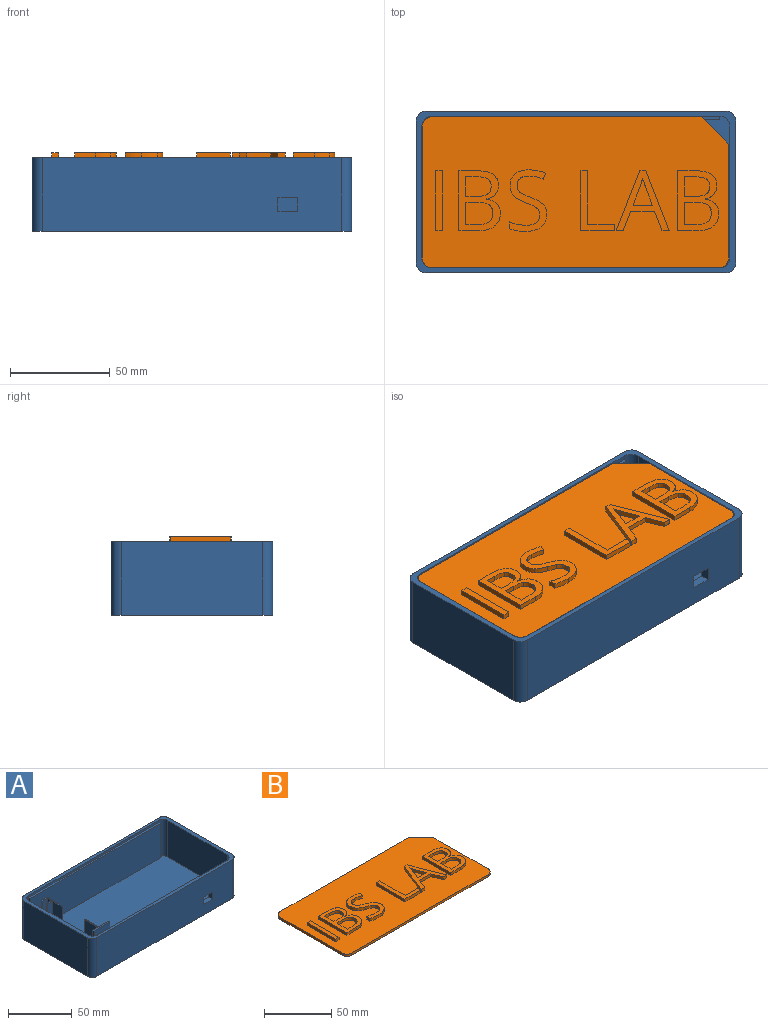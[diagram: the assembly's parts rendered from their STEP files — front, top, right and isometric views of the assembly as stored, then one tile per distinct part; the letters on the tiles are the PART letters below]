
ASSEMBLY  parts=2 mates=1
PART A: 56 faces, bbox 160x81x37 mm
  f0: plane 144x2mm, normal (0,-1,0), area 288mm2, adj f17,f23,f24,f44
  f1: plane 16.12x5.6mm, normal (0,-1,0), area 90.3mm2, adj f2,f7,f8,f42
  f2: plane 16.12x1.15mm, normal (-1,0,0), area 18.5mm2, adj f1,f8,f37,f42
  f3: plane 5.6x4.3mm, normal (0,1,0), area 24.1mm2, adj f5,f7,f39,f43
  f4: plane 154x76mm, normal (0,0,1), area 10793mm2, adj f5,f6,f19,f21,f22,f23,f24,f25
  f5: plane 58.35x30mm, normal (-1,0,0), area 231.4mm2, adj f3,f4,f8,f28,f29,f31,f32,f34
  f6: plane 30x17.4mm, normal (1,0,0), area 522mm2, adj f4,f8,f28,f35
  f7: plane 29x16.6mm, normal (-1,0,0), area 436.7mm2, adj f1,f3,f8,f29,f35,f37,f38,f39
  f8: plane 17.4x6.4mm, normal (0,0,1), area 24.8mm2, adj f1,f2,f5,f6,f7,f28,f35,f37
  f9: plane 71x37mm, normal (-1,0,0), area 2627mm2, adj f10,f16,f17,f18
  f10: cylinder r=5mm len=37mm, axis (0,0,-1), area 290.6mm2, adj f9,f11,f17,f18
  f11: plane 150x37mm, normal (0,-1,0), area 5480mm2, adj f10,f12,f17,f18,f52,f53,f54,f55
  f12: cylinder r=5mm len=37mm, axis (0,0,-1), area 290.6mm2, adj f11,f13,f17,f18
  f13: plane 71x37mm, normal (1,0,0), area 2627mm2, adj f12,f14,f17,f18
  f14: cylinder r=5mm len=37mm, axis (0,0,-1), area 290.6mm2, adj f13,f15,f17,f18
  f15: plane 150x37mm, normal (0,1,0), area 5550mm2, adj f14,f16,f17,f18
  f16: cylinder r=5mm len=37mm, axis (0,0,-1), area 290.6mm2, adj f9,f15,f17,f18
  f17: plane 160x81mm, normal (0,0,1), area 1256mm2, adj f0,f9,f10,f11,f12,f13,f14,f15
  f18: plane 160x81mm, normal (0,0,-1), area 12938.5mm2, adj f9,f10,f11,f12,f13,f14,f15,f16
  f19: cylinder r=5mm len=35mm, axis (0,0,1), area 274.9mm2, adj f4,f17,f20,f25,f50
  f20: plane 144x2mm, normal (0,1,0), area 288mm2, adj f17,f19,f21,f48
  f21: cylinder r=5mm len=35mm, axis (0,0,1), area 274.9mm2, adj f4,f17,f20,f22,f49
  f22: plane 66x35mm, normal (-1,0,0), area 2310mm2, adj f4,f17,f21,f23
  f23: cylinder r=5mm len=35mm, axis (0,0,1), area 274.9mm2, adj f0,f4,f17,f22,f46
  f24: cylinder r=5mm len=35mm, axis (0,0,1), area 274.9mm2, adj f0,f4,f17,f25,f45
  f25: plane 66x35mm, normal (1,0,0), area 2310mm2, adj f4,f17,f19,f24
  f26: plane 30x11.2mm, normal (0,1,0), area 336mm2, adj f4,f27,f33,f34
  f27: plane 30x14.9mm, normal (1,0,0), area 446.8mm2, adj f4,f26,f34,f36
  f28: plane 30x6.4mm, normal (0,1,0), area 192mm2, adj f4,f5,f6,f8
  f29: plane 5.6x2.3mm, normal (0,-1,0), area 12.9mm2, adj f5,f7,f41,f43
  f30: plane 27x14.9mm, normal (-1,0,0), area 402.2mm2, adj f31,f34,f36,f41
  f31: plane 27x5.6mm, normal (0,1,0), area 151.2mm2, adj f5,f30,f34,f41
  f32: plane 30x17.6mm, normal (0,-1,0), area 528mm2, adj f4,f5,f33,f34
  f33: plane 30x1.55mm, normal (1,0,0), area 46.5mm2, adj f4,f26,f32,f34
  f34: plane 17.6x16.44mm, normal (0,0,1), area 39.2mm2, adj f5,f26,f27,f30,f31,f32,f33,f36
  f35: plane 30x0.8mm, normal (0,-1,0), area 24mm2, adj f4,f6,f7,f8,f40
  f36: plane 30x0.8mm, normal (0,1,0), area 24mm2, adj f4,f27,f30,f34,f40
  f37: plane 16.12x5.6mm, normal (0,1,0), area 90.3mm2, adj f2,f7,f8,f42
  f38: plane 29x5.6mm, normal (0,-1,0), area 162.4mm2, adj f5,f7,f8,f39
  f39: plane 5.6x4.85mm, normal (0,0,1), area 27.2mm2, adj f3,f5,f7,f38
  f40: plane 24.51x3mm, normal (1,0,0), area 73.5mm2, adj f4,f35,f36,f41
  f41: plane 50x5.6mm, normal (0,0,1), area 280mm2, adj f5,f7,f29,f30,f31,f40
  f42: plane 5.6x1.15mm, normal (0,0,-1), area 6.4mm2, adj f1,f2,f7,f37
  f43: plane 5.6x1.15mm, normal (0,0,1), area 6.4mm2, adj f3,f5,f7,f29
  f44: plane 144x1.8mm, normal (0,0,1), area 259.2mm2, adj f0,f45,f46,f47
  f45: plane 33x1.8mm, normal (-1,0,0), area 59.4mm2, adj f4,f24,f44,f47
  f46: plane 33x1.8mm, normal (1,0,0), area 59.4mm2, adj f4,f23,f44,f47
  f47: plane 144x33mm, normal (0,-1,0), area 4752mm2, adj f4,f44,f45,f46
  f48: plane 144x1.8mm, normal (0,0,1), area 259.2mm2, adj f20,f49,f50,f51
  f49: plane 33x1.8mm, normal (1,0,0), area 59.4mm2, adj f4,f21,f48,f51
  f50: plane 33x1.8mm, normal (-1,0,0), area 59.4mm2, adj f4,f19,f48,f51
  f51: plane 144x33mm, normal (0,1,0), area 4682mm2, adj f4,f48,f49,f50,f52,f53,f54,f55
  f52: plane 7x4.3mm, normal (-1,0,0), area 30.1mm2, adj f11,f51,f53,f55
  f53: plane 10x4.3mm, normal (0,0,-1), area 43mm2, adj f11,f51,f52,f54
  f54: plane 7x4.3mm, normal (1,0,0), area 30.1mm2, adj f11,f51,f53,f55
  f55: plane 10x4.3mm, normal (0,0,1), area 43mm2, adj f11,f51,f52,f54
PART B: 119 faces, bbox 153.6x75.6x4.5 mm
  f0: plane 153.6x75.6mm, normal (0,0,1), area 9639.9mm2, adj f1,f2,f3,f4,f5,f6,f7,f8
  f1: plane 65.6x2mm, normal (-1,0,0), area 131.2mm2, adj f0,f2,f8,f9
  f2: cylinder r=5mm len=5mm, axis (0,0,-1), area 15.7mm2, adj f0,f1,f3,f9
  f3: plane 143.6x2mm, normal (0,-1,0), area 287.2mm2, adj f0,f2,f4,f9
  f4: cylinder r=5mm len=5mm, axis (0,0,-1), area 15.7mm2, adj f0,f3,f5,f9
  f5: plane 57.03x2mm, normal (1,0,0), area 114.1mm2, adj f0,f4,f6,f9
  f6: plane 13.57x13.32mm, normal (0.71,0.7,0), area 38mm2, adj f0,f5,f7,f9
  f7: plane 135.28x2mm, normal (0,1,0), area 270.6mm2, adj f0,f6,f8,f9
  f8: cylinder r=5mm len=5mm, axis (0,0,-1), area 15.7mm2, adj f0,f1,f7,f9
  f9: plane 153.6x75.6mm, normal (0,0,-1), area 11505.7mm2, adj f1,f2,f3,f4,f5,f6,f7,f8
  f10: plane 3.48x2.5mm, normal (0,-1,0), area 8.7mm2, adj f0,f11,f13,f14
  f11: plane 29.94x2.5mm, normal (1,0,0), area 74.9mm2, adj f0,f10,f12,f14
  f12: plane 3.48x2.5mm, normal (0,1,0), area 8.7mm2, adj f0,f11,f13,f14
  f13: plane 29.94x2.5mm, normal (-1,0,0), area 74.9mm2, adj f0,f10,f12,f14
  f14: plane 29.94x3.48mm, normal (0,0,1), area 104.2mm2, adj f10,f11,f12,f13
  f15: plane 29.94x2.5mm, normal (-1,0,0), area 74.9mm2, adj f0,f16,f39,f40
  f16: plane 10.45x2.5mm, normal (0,-1,0), area 26.1mm2, adj f0,f15,f17,f40
  f17: extruded ~7.59x2.5mm, area 20.2mm2, adj f0,f16,f18,f40
  f18: extruded ~6.27x2.71mm, area 17.7mm2, adj f0,f17,f19,f40
  f19: extruded ~7.17x6.82mm, area 27.4mm2, adj f0,f18,f20,f40
  f20: plane 2.5x0.2mm, normal (1,0,0), area 0.5mm2, adj f0,f19,f21,f40
  f21: extruded ~4.34x2.5mm, area 12.4mm2, adj f0,f20,f22,f40
  f22: extruded ~4.4x2.5mm, area 11.9mm2, adj f0,f21,f23,f40
  f23: extruded ~5.63x2.66mm, area 16.3mm2, adj f0,f22,f24,f40
  f24: extruded ~8.62x2.5mm, area 22.3mm2, adj f0,f23,f39,f40
  f25: plane 9.8x2.5mm, normal (1,0,0), area 24.5mm2, adj f26,f37,f40,f42
  f26: plane 5.12x2.5mm, normal (0,-1,0), area 12.8mm2, adj f25,f27,f40,f42
  f27: extruded ~5.73x2.5mm, area 14.8mm2, adj f26,f28,f40,f42
  f28: extruded ~3.64x2.5mm, area 10.6mm2, adj f27,f29,f40,f42
  f29: extruded ~3.9x2.5mm, area 11mm2, adj f28,f30,f40,f42
  f30: extruded ~5.31x2.5mm, area 13.8mm2, adj f29,f37,f40,f42
  f31: plane 5.96x2.5mm, normal (0,-1,0), area 14.9mm2, adj f32,f38,f40,f41
  f32: extruded ~5.7x2.5mm, area 14.8mm2, adj f31,f33,f40,f41
  f33: extruded ~4.1x2.5mm, area 11.7mm2, adj f32,f34,f40,f41
  f34: extruded ~4.4x2.5mm, area 12.4mm2, adj f33,f35,f40,f41
  f35: extruded ~5.46x2.5mm, area 14.3mm2, adj f34,f36,f40,f41
  f36: plane 6.25x2.5mm, normal (0,1,0), area 15.6mm2, adj f35,f38,f40,f41
  f37: plane 5.73x2.5mm, normal (0,1,0), area 14.3mm2, adj f25,f30,f40,f42
  f38: plane 11.21x2.5mm, normal (1,0,0), area 28mm2, adj f31,f36,f40,f41
  f39: plane 8.46x2.5mm, normal (0,1,0), area 21.2mm2, adj f0,f15,f24,f40
  f40: plane 29.94x20.75mm, normal (0,0,1), area 305.7mm2, adj f15,f16,f17,f18,f19,f20,f21,f22
  f41: plane 13.54x11.21mm, normal (0,0,1), area 138.2mm2, adj f31,f32,f33,f34,f35,f36,f38
  f42: plane 12.66x9.8mm, normal (0,0,1), area 113.4mm2, adj f25,f26,f27,f28,f29,f30,f37
  f43: extruded ~4.99x2.5mm, area 13.6mm2, adj f0,f44,f67,f68
  f44: extruded ~6.48x3.6mm, area 18.7mm2, adj f0,f43,f45,f68
  f45: extruded ~4.17x2.5mm, area 11.4mm2, adj f0,f44,f46,f68
  f46: extruded ~2.5x1.94mm, area 6.7mm2, adj f0,f45,f47,f68
  f47: extruded ~2.55x2.5mm, area 6.6mm2, adj f0,f46,f48,f68
  f48: extruded ~3.3x2.5mm, area 9.5mm2, adj f0,f47,f49,f68
  f49: extruded ~4.32x2.5mm, area 11.4mm2, adj f0,f48,f50,f68
  f50: extruded ~7.21x2.5mm, area 18.6mm2, adj f0,f49,f51,f68
  f51: plane 3.03x2.5mm, normal (0.94,-0.34,0), area 8mm2, adj f0,f50,f52,f68
  f52: extruded ~8.21x2.5mm, area 21.1mm2, adj f0,f51,f53,f68
  f53: extruded ~6.88x2.5mm, area 18.3mm2, adj f0,f52,f54,f68
  f54: extruded ~5.51x2.6mm, area 15.8mm2, adj f0,f53,f55,f68
  f55: extruded ~5.34x2.5mm, area 14.4mm2, adj f0,f54,f56,f68
  f56: extruded ~5.97x3.54mm, area 17.5mm2, adj f0,f55,f57,f68
  f57: extruded ~4.45x2.5mm, area 12.1mm2, adj f0,f56,f58,f68
  f58: extruded ~2.5x2.09mm, area 7mm2, adj f0,f57,f59,f68
  f59: extruded ~2.55x2.5mm, area 6.6mm2, adj f0,f58,f60,f68
  f60: extruded ~3.68x2.5mm, area 10.6mm2, adj f0,f59,f61,f68
  f61: extruded ~5.24x2.5mm, area 13.7mm2, adj f0,f60,f62,f68
  f62: extruded ~4.3x2.5mm, area 10.8mm2, adj f0,f61,f63,f68
  f63: extruded ~4.02x2.5mm, area 10.5mm2, adj f0,f62,f64,f68
  f64: plane 3.36x2.5mm, normal (-1,0,0), area 8.4mm2, adj f0,f63,f65,f68
  f65: extruded ~8.19x2.5mm, area 20.9mm2, adj f0,f64,f66,f68
  f66: extruded ~7.78x2.5mm, area 20.6mm2, adj f0,f65,f67,f68
  f67: extruded ~6.17x2.87mm, area 17.7mm2, adj f0,f43,f66,f68
  f68: plane 30.78x18.84mm, normal (0,0,1), area 207.5mm2, adj f43,f44,f45,f46,f47,f48,f49,f50
  f69: plane 16.69x2.5mm, normal (0,-1,0), area 41.7mm2, adj f0,f70,f74,f75
  f70: plane 3.15x2.5mm, normal (1,0,0), area 7.9mm2, adj f0,f69,f71,f75
  f71: plane 13.21x2.5mm, normal (0,1,0), area 33mm2, adj f0,f70,f72,f75
  f72: plane 26.79x2.5mm, normal (1,0,0), area 67mm2, adj f0,f71,f73,f75
  f73: plane 3.48x2.5mm, normal (0,1,0), area 8.7mm2, adj f0,f72,f74,f75
  f74: plane 29.94x2.5mm, normal (-1,0,0), area 74.9mm2, adj f0,f69,f73,f75
  f75: plane 29.94x16.69mm, normal (0,0,1), area 145.8mm2, adj f69,f70,f71,f72,f73,f74
  f76: plane 3.6x2.5mm, normal (0,-1,0), area 9mm2, adj f0,f77,f88,f89
  f77: plane 30.07x11.78mm, normal (0.93,0.36,0), area 80.7mm2, adj f0,f76,f78,f89
  f78: plane 2.93x2.5mm, normal (0,1,0), area 7.3mm2, adj f0,f77,f79,f89
  f79: plane 30.07x11.84mm, normal (-0.93,0.37,0), area 80.8mm2, adj f0,f78,f80,f89
  f80: plane 3.53x2.5mm, normal (0,-1,0), area 8.8mm2, adj f0,f79,f81,f89
  f81: plane 9.52x3.68mm, normal (0.93,-0.36,0), area 25.5mm2, adj f0,f80,f82,f89
  f82: plane 12x2.5mm, normal (0,-1,0), area 30mm2, adj f0,f81,f88,f89
  f83: plane 9.69x2.5mm, normal (0,1,0), area 24.2mm2, adj f84,f87,f89,f90
  f84: plane 9.28x3.52mm, normal (0.94,-0.35,0), area 24.8mm2, adj f83,f85,f89,f90
  f85: extruded ~4.32x2.5mm, area 11.3mm2, adj f84,f86,f89,f90
  f86: extruded ~4.32x2.5mm, area 11.3mm2, adj f85,f87,f89,f90
  f87: plane 9.28x3.49mm, normal (-0.94,-0.35,0), area 24.8mm2, adj f83,f86,f89,f90
  f88: plane 9.52x3.73mm, normal (-0.93,-0.36,0), area 25.6mm2, adj f0,f76,f82,f89
  f89: plane 30.07x26.54mm, normal (0,0,1), area 230.7mm2, adj f76,f77,f78,f79,f80,f81,f82,f83
  f90: plane 13.6x9.69mm, normal (0,0,1), area 62.8mm2, adj f83,f84,f85,f86,f87
  f91: plane 29.94x2.5mm, normal (-1,0,0), area 74.9mm2, adj f0,f92,f115,f116
  f92: plane 10.45x2.5mm, normal (0,-1,0), area 26.1mm2, adj f0,f91,f93,f116
  f93: extruded ~7.59x2.5mm, area 20.2mm2, adj f0,f92,f94,f116
  f94: extruded ~6.27x2.71mm, area 17.7mm2, adj f0,f93,f95,f116
  f95: extruded ~7.17x6.82mm, area 27.4mm2, adj f0,f94,f96,f116
  f96: plane 2.5x0.2mm, normal (1,0,0), area 0.5mm2, adj f0,f95,f97,f116
  f97: extruded ~4.34x2.5mm, area 12.4mm2, adj f0,f96,f98,f116
  f98: extruded ~4.4x2.5mm, area 11.9mm2, adj f0,f97,f99,f116
  f99: extruded ~5.63x2.66mm, area 16.3mm2, adj f0,f98,f100,f116
  f100: extruded ~8.62x2.5mm, area 22.3mm2, adj f0,f99,f115,f116
  f101: plane 9.8x2.5mm, normal (1,0,0), area 24.5mm2, adj f102,f113,f116,f118
  f102: plane 5.12x2.5mm, normal (0,-1,0), area 12.8mm2, adj f101,f103,f116,f118
  f103: extruded ~5.73x2.5mm, area 14.8mm2, adj f102,f104,f116,f118
  f104: extruded ~3.64x2.5mm, area 10.6mm2, adj f103,f105,f116,f118
  f105: extruded ~3.9x2.5mm, area 11mm2, adj f104,f106,f116,f118
  f106: extruded ~5.31x2.5mm, area 13.8mm2, adj f105,f113,f116,f118
  f107: plane 5.96x2.5mm, normal (0,-1,0), area 14.9mm2, adj f108,f114,f116,f117
  f108: extruded ~5.7x2.5mm, area 14.8mm2, adj f107,f109,f116,f117
  f109: extruded ~4.1x2.5mm, area 11.7mm2, adj f108,f110,f116,f117
  f110: extruded ~4.4x2.5mm, area 12.4mm2, adj f109,f111,f116,f117
  f111: extruded ~5.46x2.5mm, area 14.3mm2, adj f110,f112,f116,f117
  f112: plane 6.25x2.5mm, normal (0,1,0), area 15.6mm2, adj f111,f114,f116,f117
  f113: plane 5.73x2.5mm, normal (0,1,0), area 14.3mm2, adj f101,f106,f116,f118
  f114: plane 11.21x2.5mm, normal (1,0,0), area 28mm2, adj f107,f112,f116,f117
  f115: plane 8.46x2.5mm, normal (0,1,0), area 21.2mm2, adj f0,f91,f100,f116
  f116: plane 29.94x20.75mm, normal (0,0,1), area 305.7mm2, adj f91,f92,f93,f94,f95,f96,f97,f98
  f117: plane 13.54x11.21mm, normal (0,0,1), area 138.2mm2, adj f107,f108,f109,f110,f111,f112,f114
  f118: plane 12.66x9.8mm, normal (0,0,1), area 113.4mm2, adj f101,f102,f103,f104,f105,f106,f113
PLACE A t=(-55.11,20.14,-13.43)mm
PLACE B t=(-46.24,121.56,-13.43)mm
MATE planar B.f0 <-> A.f17  axis (0,0,1) through (-127.29,-17.89,23.57)mm
